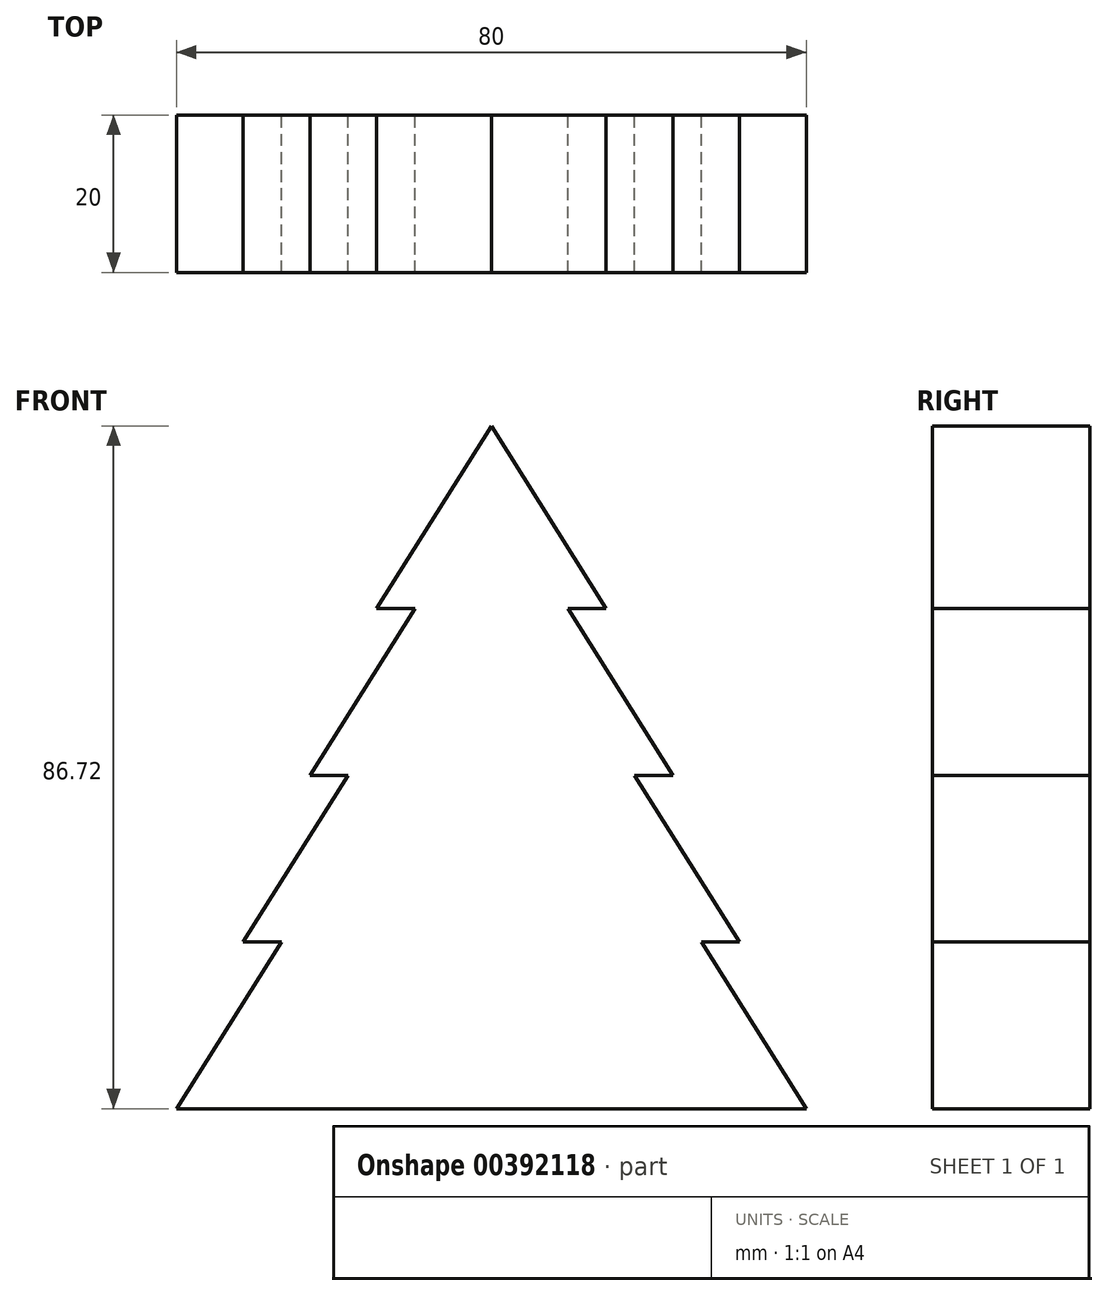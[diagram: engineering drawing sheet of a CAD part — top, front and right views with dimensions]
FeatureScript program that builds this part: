
annotation { "Feature Type Name" : "Feature", "Feature Type Description" : "" }
export const myFeature = defineFeature(function(context is Context, id is Id, definition is map)
    precondition{}
    {
        {
            var Q0;
            Q0=qCreatedBy(makeId("Front.planeOp"),FACE);
            var sketch = newSketch(context, id + "F0", { "sketchPlane" : qUnion([Q0])});
            skLineSegment(sketch, "E0", {"start": v(0, 100) * mm, "end": v(0, 0) * mm, "construction": true});
            skLineSegment(sketch, "E1", {"start": v(0, 0) * mm, "end": v(40, 0) * mm});
            skLineSegment(sketch, "E2", {"start": v(0, 100) * mm, "end": v(40, 0) * mm, "construction": true});
            skLineSegment(sketch, "E3", {"start": v(40, 0) * mm, "end": v(26.67, 21.18) * mm});
            skLineSegment(sketch, "E4", {"start": v(26.67, 21.18) * mm, "end": v(31.53, 21.18) * mm});
            skLineSegment(sketch, "E5", {"start": v(31.53, 21.18) * mm, "end": v(18.2, 42.36) * mm});
            skLineSegment(sketch, "E6", {"start": v(18.2, 42.36) * mm, "end": v(23.06, 42.36) * mm});
            skLineSegment(sketch, "E7", {"start": v(23.06, 42.36) * mm, "end": v(9.73, 63.54) * mm});
            skLineSegment(sketch, "E8", {"start": v(9.73, 63.54) * mm, "end": v(14.58, 63.54) * mm});
            skLineSegment(sketch, "E9", {"start": v(14.58, 63.54) * mm, "end": v(0, 86.72) * mm});
            skLineSegment(sketch, "E10", {"start": v(0, 0) * mm, "end": v(0, 86.72) * mm});
            skSolve(sketch);
        }
        {
            var Q0;
            Q0=qSketchRegion(id+"F0",true);
            extrude(context, id + "F1", {"entities" : qUnion([Q0]), "depth" : 20 * mm});
        }
        {
            var Q0;
            Q0=makeQuery(id+"F1.opExtrude","SWEPT_BODY",BODY,{"disambiguationData":[OSD([sQuery(id+"F0.wireOp",EDGE,"E1"),sQuery(id+"F0.wireOp",EDGE,"E3"),sQuery(id+"F0.wireOp",EDGE,"E4"),sQuery(id+"F0.wireOp",EDGE,"E5"),sQuery(id+"F0.wireOp",EDGE,"E6"),sQuery(id+"F0.wireOp",EDGE,"E7"),sQuery(id+"F0.wireOp",EDGE,"E8"),sQuery(id+"F0.wireOp",EDGE,"E9"),sQuery(id+"F0.wireOp",EDGE,"E10")])]});
            var Q1;
            Q1=qCreatedBy(makeId("Right.planeOp"),FACE);
            mirror(context, id + "F2", {"operationType" : NewBodyOperationType.ADD, "entities" : qUnion([Q0]), "mirrorPlane" : qUnion([Q1])});
        }
    });
